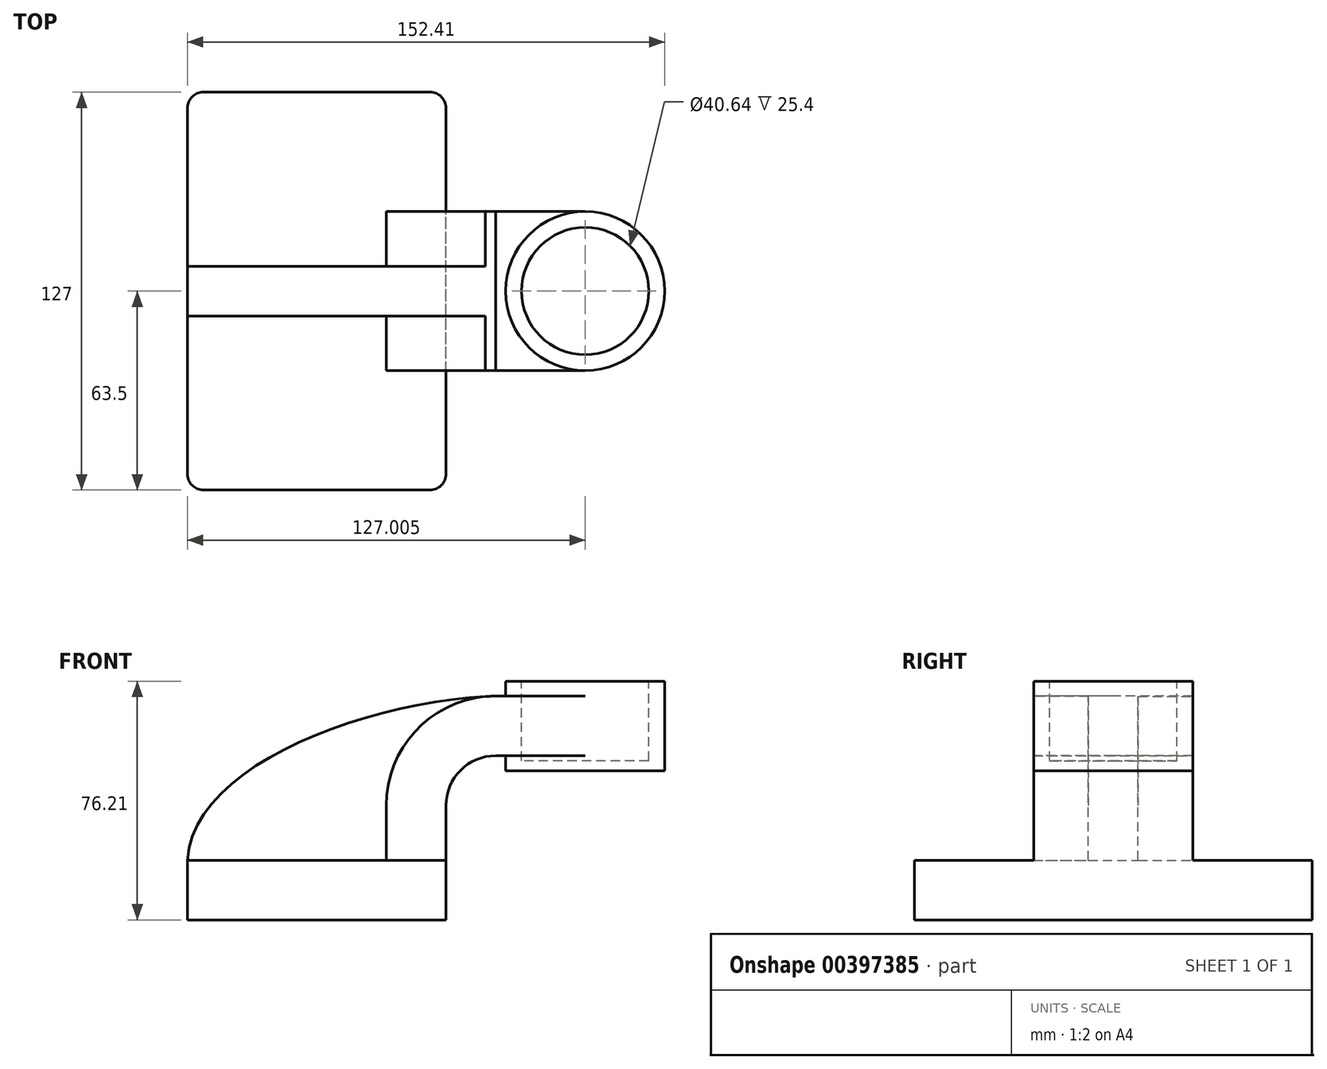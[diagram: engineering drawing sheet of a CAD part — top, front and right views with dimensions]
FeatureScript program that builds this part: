
annotation { "Feature Type Name" : "Feature", "Feature Type Description" : "" }
export const myFeature = defineFeature(function(context is Context, id is Id, definition is map)
    precondition{}
    {
        {
            var Q0;
            Q0=qCreatedBy(makeId("Front.planeOp"),FACE);
            var sketch = newSketch(context, id + "F0", { "sketchPlane" : qUnion([Q0])});
            skLineSegment(sketch, "E0.rect.bottom", {"start": v(-41.28, 9.52) * mm, "end": v(41.28, 9.52) * mm});
            skLineSegment(sketch, "E0.rect.top", {"start": v(-41.28, -9.52) * mm, "end": v(41.28, -9.52) * mm});
            skLineSegment(sketch, "E0.rect.left", {"start": v(-41.28, 9.52) * mm, "end": v(-41.28, -9.52) * mm});
            skLineSegment(sketch, "E0.rect.right", {"start": v(41.28, 9.52) * mm, "end": v(41.28, -9.52) * mm});
            skPoint(sketch, "E0.rect.middle", {"position": v(0, 0) * mm});
            skLineSegment(sketch, "E1", {"start": v(41.28, 9.52) * mm, "end": v(41.28, 27) * mm});
            skArc(sketch, "E2", {"start": v(41.28, 27) * mm, "mid": v(45.92, 38.23) * mm, "end": v(57.15, 42.88) * mm});
            skLineSegment(sketch, "E3", {"start": v(57.15, 42.88) * mm, "end": v(85.72, 42.88) * mm});
            skLineSegment(sketch, "E4.rect.bottom", {"start": v(60.32, 38.1) * mm, "end": v(111.12, 38.1) * mm});
            skLineSegment(sketch, "E4.rect.top", {"start": v(60.32, 66.68) * mm, "end": v(111.12, 66.68) * mm});
            skLineSegment(sketch, "E4.rect.left", {"start": v(60.32, 38.1) * mm, "end": v(60.32, 66.68) * mm});
            skLineSegment(sketch, "E4.rect.right", {"start": v(111.13, 38.1) * mm, "end": v(111.12, 66.68) * mm});
            skPoint(sketch, "E4.rect.middle", {"position": v(85.72, 52.39) * mm});
            skLineSegment(sketch, "E5.0", {"start": v(57.15, 61.93) * mm, "end": v(85.72, 61.93) * mm});
            skArc(sketch, "E5.1", {"start": v(22.23, 27) * mm, "mid": v(32.45, 51.7) * mm, "end": v(57.15, 61.93) * mm});
            skLineSegment(sketch, "E5.2", {"start": v(22.23, 9.52) * mm, "end": v(22.23, 27) * mm});
            skLineSegment(sketch, "E6", {"start": v(85.72, 38.1) * mm, "end": v(85.72, 66.68) * mm});
            skFitSpline(sketch, "E7", {"points": [v(-41.28, 9.53) * mm, v(57.15, 61.93) * mm], "startDerivative": vector(5.2, 92.34) * mm, "endDerivative": vector(120.92, 4.22) * mm});
            skSolve(sketch);
        }
        {
            var Q0;
            Q0=makeQuery(id+"F0.imprint","IMPRINT",FACE,{"disambiguationData":[TD([[makeQuery(id+"F0.imprint","IMPRINT",EDGE,{"derivedFrom":sQuery(id+"F0.wireOp",EDGE,"E0.rect.top")}),1.0]])]});
            extrude(context, id + "F1", {"entities" : qUnion([Q0]), "endBound" : BoundingType.SYMMETRIC, "depth" : 127 * mm});
        }
        {
            var Q0;
            {var subQ9=sQuery(id+"F0.wireOp",EDGE,"E1");Q0=makeQuery(id+"F0.imprint","IMPRINT",FACE,{"disambiguationData":[TD([[makeQuery(id+"F0.imprint","IMPRINT",EDGE,{"derivedFrom":subQ9}),1.0]])]});}
            var Q1;
            {var subQ0=sQuery(id+"F0.wireOp",EDGE,"E6");var subQ1=sQuery(id+"F0.wireOp",EDGE,"E3");var subQ2=makeQuery(id+"F0.imprint","INTERSECT",VERTEX,{"derivedFrom":[subQ1,subQ0]});Q1=makeQuery(id+"F0.imprint","IMPRINT",FACE,{"disambiguationData":[TD([[makeQuery(id+"F0.imprint","IMPRINT",EDGE,{"disambiguationData":[TD([[subQ2,1.0]])],"derivedFrom":subQ1}),1.0]])]});}
            extrude(context, id + "F2", {"entities" : qUnion([Q0, Q1]), "operationType" : NewBodyOperationType.ADD, "endBound" : BoundingType.SYMMETRIC, "depth" : 50.8 * mm});
        }
        {
            var Q0;
            {var subQ3=sQuery(id+"F0.wireOp",EDGE,"E5.2");Q0=makeQuery(id+"F0.imprint","IMPRINT",FACE,{"disambiguationData":[TD([[makeQuery(id+"F0.imprint","IMPRINT",EDGE,{"derivedFrom":subQ3}),1.0]])]});}
            extrude(context, id + "F3", {"entities" : qUnion([Q0]), "operationType" : NewBodyOperationType.ADD, "endBound" : BoundingType.SYMMETRIC, "depth" : 15.88 * mm});
        }
        {
            var Q0;
            {var subQ5=sQuery(id+"F0.wireOp",EDGE,"E4.rect.right");Q0=makeQuery(id+"F0.imprint","IMPRINT",FACE,{"disambiguationData":[TD([[makeQuery(id+"F0.imprint","IMPRINT",EDGE,{"derivedFrom":subQ5}),1.0]])]});}
            var Q1;
            Q1=sQuery(id+"F0.wireOp",EDGE,"E6");
            revolve(context, id + "F4", {"operationType" : NewBodyOperationType.ADD, "entities" : qUnion([Q0]), "axis" : qUnion([Q1]), "revolveType" : RevolveType.FULL});
        }
        {
            var Q0;
            Q0=makeQuery(id+"F1.opExtrude","CAP_EDGE",EDGE,{"disambiguationData":[OSD([sQuery(id+"F0.wireOp",EDGE,"E0.rect.right")])],"isStart":false});
            var Q1;
            Q1=makeQuery(id+"F1.opExtrude","CAP_EDGE",EDGE,{"disambiguationData":[OSD([sQuery(id+"F0.wireOp",EDGE,"E0.rect.left")])],"isStart":false});
            var Q2;
            Q2=makeQuery(id+"F1.opExtrude","CAP_EDGE",EDGE,{"disambiguationData":[OSD([sQuery(id+"F0.wireOp",EDGE,"E0.rect.right")])],"isStart":true});
            var Q3;
            Q3=makeQuery(id+"F1.opExtrude","CAP_EDGE",EDGE,{"disambiguationData":[OSD([sQuery(id+"F0.wireOp",EDGE,"E0.rect.left")])],"isStart":true});
            fillet(context, id + "F5", {"entities" : qUnion([Q0, Q1, Q2, Q3]), "radius" : 5.08 * mm, "tangentPropagation" : true, "allowEdgeOverflow" : false});
        }
        {
            var Q0;
            Q0=makeQuery(id+"F4.opRevolve","SWEPT_FACE",FACE,{"disambiguationData":[OSD([sQuery(id+"F0.wireOp",EDGE,"E4.rect.top")])]});
            var sketch = newSketch(context, id + "F6", { "sketchPlane" : qUnion([Q0])});
            skCircle(sketch, "E8.0", {"center": v(85.72, 0) * mm, "radius": 20.32 * mm});
            skSolve(sketch);
        }
        {
            var Q0;
            Q0=makeQuery(id+"F6.imprint","IMPRINT",FACE,{"disambiguationData":[TD([[makeQuery(id+"F6.imprint","IMPRINT",EDGE,{"derivedFrom":sQuery(id+"F6.wireOp",EDGE,"E8.0")}),1.0]])]});
            extrude(context, id + "F7", {"entities" : qUnion([Q0]), "operationType" : NewBodyOperationType.REMOVE, "depth" : -25.4 * mm});
        }
    });
